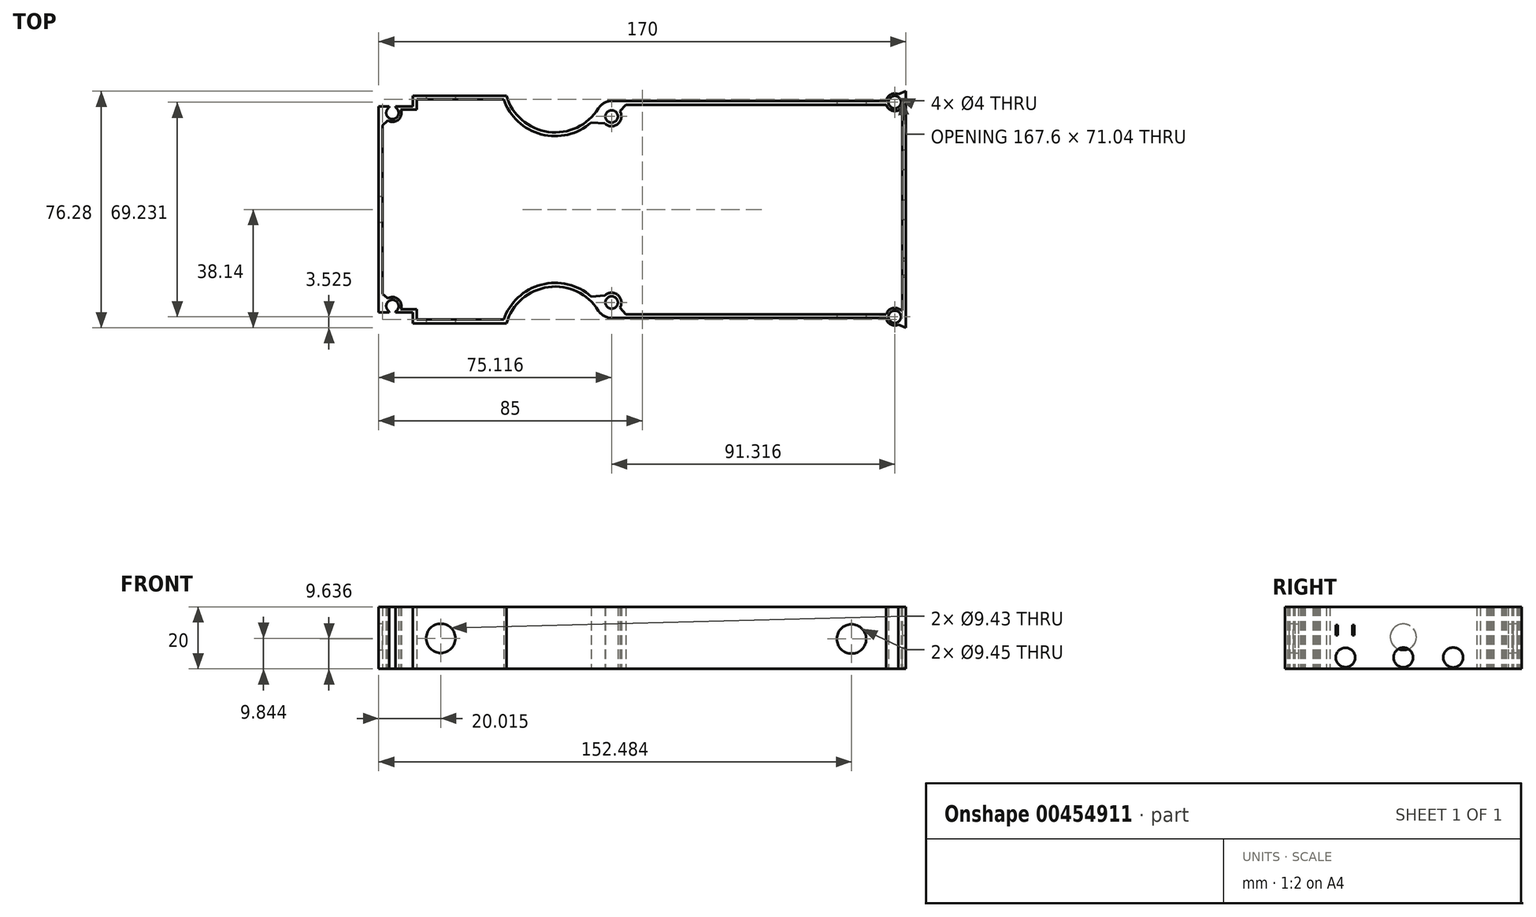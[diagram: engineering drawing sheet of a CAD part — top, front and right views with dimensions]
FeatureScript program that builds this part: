
annotation { "Feature Type Name" : "Feature", "Feature Type Description" : "" }
export const myFeature = defineFeature(function(context is Context, id is Id, definition is map)
    precondition{}
    {
        {
            var Q0;
            Q0=qCreatedBy(makeId("Top.planeOp"),FACE);
            var sketch = newSketch(context, id + "F0", { "sketchPlane" : qUnion([Q0])});
            skLineSegment(sketch, "E0", {"start": v(-2.46, 0) * mm, "end": v(-170, 0) * mm, "construction": true});
            skLineSegment(sketch, "E1.MirrorCS", {"start": v(-164.65, 32.92) * mm, "end": v(-164.65, 33.2) * mm});
            skLineSegment(sketch, "E2.MirrorCS", {"start": v(-166.56, 32.9) * mm, "end": v(-166.56, 33.2) * mm});
            skArc(sketch, "E3.MirrorCS", {"start": v(-5.4, 33.8) * mm, "mid": v(-3.57, 32.62) * mm, "end": v(-1.74, 33.8) * mm});
            skArc(sketch, "E4.MirrorCS", {"start": v(-1.63, 35.13) * mm, "mid": v(-3.57, 36.62) * mm, "end": v(-5.5, 35.13) * mm});
            skLineSegment(sketch, "E5.MirrorCS", {"start": v(-164.65, 33.2) * mm, "end": v(-163.23, 33.2) * mm});
            skLineSegment(sketch, "E6.MirrorCS", {"start": v(-1.2, 32.52) * mm, "end": v(-1.54, 32.57) * mm});
            skCircle(sketch, "E7.MirrorC", {"center": v(-3.57, 34.62) * mm, "radius": 2 * mm});
            skLineSegment(sketch, "E8.MirrorCS", {"start": v(-167.22, 28.48) * mm, "end": v(-167, 28.62) * mm});
            skCircle(sketch, "E9.MirrorC", {"center": v(-94.88, 30) * mm, "radius": 2 * mm});
            skLineSegment(sketch, "E10.MirrorCS", {"start": v(-167.22, 28.48) * mm, "end": v(-168.8, 27.19) * mm});
            skLineSegment(sketch, "E11.MirrorCS", {"start": v(-159, 36.72) * mm, "end": v(-157.8, 36.72) * mm});
            skLineSegment(sketch, "E12.MirrorCS", {"start": v(0, 38.14) * mm, "end": v(0, 35) * mm});
            skLineSegment(sketch, "E13.MirrorCS", {"start": v(-159, 33.2) * mm, "end": v(-159, 36.72) * mm});
            skLineSegment(sketch, "E14.MirrorCS", {"start": v(-155.88, 35.52) * mm, "end": v(-157.8, 35.52) * mm});
            skArc(sketch, "E15.MirrorCS", {"start": v(-166.56, 32.9) * mm, "mid": v(-165.57, 29.15) * mm, "end": v(-164.65, 32.92) * mm});
            skArc(sketch, "E16.MirrorCS", {"start": v(-94.88, 35) * mm, "mid": v(-97.32, 34.37) * mm, "end": v(-99.14, 32.63) * mm});
            skArc(sketch, "E17.MirrorCS", {"start": v(-162.9, 32.23) * mm, "mid": v(-163.68, 28.97) * mm, "end": v(-167, 28.62) * mm});
            skLineSegment(sketch, "E18.MirrorCS", {"start": v(-157.8, 32.23) * mm, "end": v(-162.9, 32.23) * mm});
            skLineSegment(sketch, "E19.MirrorCS", {"start": v(-2.47, 37.17) * mm, "end": v(0, 38.14) * mm});
            skLineSegment(sketch, "E20.MirrorCS", {"start": v(-163.23, 33.2) * mm, "end": v(-159, 33.2) * mm});
            skLineSegment(sketch, "E21.MirrorCS", {"start": v(-157.8, 35.52) * mm, "end": v(-157.8, 32.23) * mm});
            skLineSegment(sketch, "E22.MirrorCS", {"start": v(-170, 33.2) * mm, "end": v(-166.56, 33.2) * mm});
            skLineSegment(sketch, "E23.MirrorCS", {"start": v(-92.23, 31.68) * mm, "end": v(-90.26, 33.8) * mm});
            skLineSegment(sketch, "E24.MirrorCS", {"start": v(-97.1, 27.76) * mm, "end": v(-101.46, 28.05) * mm});
            skLineSegment(sketch, "E25.MirrorCS", {"start": v(-94.88, 35) * mm, "end": v(-6.33, 35) * mm});
            skPoint(sketch, "E26.MirrorP", {"position": v(-170, 36.72) * mm});
            skLineSegment(sketch, "E27.MirrorCS", {"start": v(-90.26, 33.8) * mm, "end": v(-6.33, 33.8) * mm});
            skArc(sketch, "E28.MirrorCS", {"start": v(-97.1, 27.76) * mm, "mid": v(-92.91, 27.55) * mm, "end": v(-92.23, 31.68) * mm});
            skLineSegment(sketch, "E29.MirrorCS", {"start": v(-128.81, 36.72) * mm, "end": v(-157.8, 36.72) * mm});
            skLineSegment(sketch, "E30.MirrorCS", {"start": v(-129.69, 35.52) * mm, "end": v(-155.88, 35.52) * mm});
            skArc(sketch, "E31.MirrorCS", {"start": v(-128.81, 36.72) * mm, "mid": v(-115.3, 25.02) * mm, "end": v(-99.14, 32.63) * mm});
            skPoint(sketch, "E32.MirrorP", {"position": v(-160.88, 35.52) * mm});
            skPoint(sketch, "E33.MirrorP", {"position": v(-97.92, 35) * mm});
            skPoint(sketch, "E34.MirrorP", {"position": v(-166.61, 33.2) * mm});
            skLineSegment(sketch, "E35.MirrorCS", {"start": v(0, 35) * mm, "end": v(0, 0) * mm});
            skLineSegment(sketch, "E36.MirrorCS", {"start": v(-168.8, 0) * mm, "end": v(-168.8, 27.19) * mm});
            skLineSegment(sketch, "E37.MirrorCS", {"start": v(-1.2, 32.52) * mm, "end": v(-1.2, 0) * mm});
            skLineSegment(sketch, "E38.MirrorCS", {"start": v(-170, 0) * mm, "end": v(-170, 33.2) * mm});
            skArc(sketch, "E39.MirrorCS", {"start": v(-129.69, 35.52) * mm, "mid": v(-117.57, 24.25) * mm, "end": v(-101.46, 28.05) * mm});
            skArc(sketch, "E40", {"start": v(-6.33, 35) * mm, "mid": v(-4.94, 37.04) * mm, "end": v(-2.47, 37.17) * mm});
            skArc(sketch, "E41", {"start": v(-6.33, 33.8) * mm, "mid": v(-4.28, 31.83) * mm, "end": v(-1.54, 32.57) * mm});
            skPoint(sketch, "E42.orphan", {"position": v(-5.66, 35) * mm});
            skPoint(sketch, "E43.orphan", {"position": v(-5.54, 33.8) * mm});
            skPoint(sketch, "E44.orphan", {"position": v(-2.57, 32.73) * mm});
            skPoint(sketch, "E45.orphan", {"position": v(-3.57, 36.75) * mm});
            skArc(sketch, "E46.MirrorCS", {"start": v(-1.63, -35.13) * mm, "mid": v(-3.57, -36.62) * mm, "end": v(-5.5, -35.13) * mm});
            skArc(sketch, "E47.MirrorCS", {"start": v(-5.4, -33.8) * mm, "mid": v(-3.57, -32.62) * mm, "end": v(-1.74, -33.8) * mm});
            skLineSegment(sketch, "E48.MirrorCS", {"start": v(-164.65, -32.92) * mm, "end": v(-164.65, -33.2) * mm});
            skCircle(sketch, "E49.MirrorC", {"center": v(-3.57, -34.62) * mm, "radius": 2 * mm});
            skLineSegment(sketch, "E50.MirrorCS", {"start": v(-1.2, -32.52) * mm, "end": v(-1.54, -32.57) * mm});
            skLineSegment(sketch, "E51.MirrorCS", {"start": v(-164.65, -33.2) * mm, "end": v(-163.23, -33.2) * mm});
            skLineSegment(sketch, "E52.MirrorCS", {"start": v(-166.56, -32.9) * mm, "end": v(-166.56, -33.2) * mm});
            skArc(sketch, "E53.MirrorCS", {"start": v(-6.33, -33.8) * mm, "mid": v(-4.28, -31.83) * mm, "end": v(-1.54, -32.57) * mm});
            skLineSegment(sketch, "E54.MirrorCS", {"start": v(-163.23, -33.2) * mm, "end": v(-159, -33.2) * mm});
            skLineSegment(sketch, "E55.MirrorCS", {"start": v(-170, -33.2) * mm, "end": v(-166.56, -33.2) * mm});
            skLineSegment(sketch, "E56.MirrorCS", {"start": v(-157.8, -32.23) * mm, "end": v(-162.9, -32.23) * mm});
            skLineSegment(sketch, "E57.MirrorCS", {"start": v(-167.22, -28.48) * mm, "end": v(-168.8, -27.19) * mm});
            skLineSegment(sketch, "E58.MirrorCS", {"start": v(-167.22, -28.48) * mm, "end": v(-167, -28.62) * mm});
            skLineSegment(sketch, "E59.MirrorCS", {"start": v(-159, -33.2) * mm, "end": v(-159, -36.72) * mm});
            skArc(sketch, "E60.MirrorCS", {"start": v(-166.56, -32.9) * mm, "mid": v(-165.57, -29.15) * mm, "end": v(-164.65, -32.92) * mm});
            skLineSegment(sketch, "E61.MirrorCS", {"start": v(-155.88, -35.52) * mm, "end": v(-157.8, -35.52) * mm});
            skLineSegment(sketch, "E62.MirrorCS", {"start": v(-157.8, -35.52) * mm, "end": v(-157.8, -32.23) * mm});
            skLineSegment(sketch, "E63.MirrorCS", {"start": v(0, -38.14) * mm, "end": v(0, -35) * mm});
            skLineSegment(sketch, "E64.MirrorCS", {"start": v(-159, -36.72) * mm, "end": v(-157.8, -36.72) * mm});
            skCircle(sketch, "E65.MirrorC", {"center": v(-94.88, -30) * mm, "radius": 2 * mm});
            skLineSegment(sketch, "E66.MirrorCS", {"start": v(-2.47, -37.17) * mm, "end": v(0, -38.14) * mm});
            skArc(sketch, "E67.MirrorCS", {"start": v(-6.33, -35) * mm, "mid": v(-4.94, -37.04) * mm, "end": v(-2.47, -37.17) * mm});
            skArc(sketch, "E68.MirrorCS", {"start": v(-162.9, -32.23) * mm, "mid": v(-163.68, -28.97) * mm, "end": v(-167, -28.62) * mm});
            skLineSegment(sketch, "E69.MirrorCS", {"start": v(-97.1, -27.76) * mm, "end": v(-101.46, -28.05) * mm});
            skArc(sketch, "E70.MirrorCS", {"start": v(-94.88, -35) * mm, "mid": v(-97.32, -34.37) * mm, "end": v(-99.14, -32.63) * mm});
            skLineSegment(sketch, "E71.MirrorCS", {"start": v(-92.23, -31.68) * mm, "end": v(-90.26, -33.8) * mm});
            skArc(sketch, "E72.MirrorCS", {"start": v(-97.1, -27.76) * mm, "mid": v(-92.91, -27.55) * mm, "end": v(-92.23, -31.68) * mm});
            skPoint(sketch, "E73.MirrorP", {"position": v(-5.54, -33.8) * mm});
            skPoint(sketch, "E74.MirrorP", {"position": v(-97.92, -35) * mm});
            skLineSegment(sketch, "E75.MirrorCS", {"start": v(-1.2, -32.52) * mm, "end": v(-1.2, 0) * mm});
            skPoint(sketch, "E76.MirrorP", {"position": v(-5.66, -35) * mm});
            skLineSegment(sketch, "E77.MirrorCS", {"start": v(-94.88, -35) * mm, "end": v(-6.33, -35) * mm});
            skLineSegment(sketch, "E78.MirrorCS", {"start": v(-168.8, 0) * mm, "end": v(-168.8, -27.19) * mm});
            skPoint(sketch, "E79.MirrorP", {"position": v(-160.88, -35.52) * mm});
            skPoint(sketch, "E80.MirrorP", {"position": v(-170, -36.72) * mm});
            skPoint(sketch, "E81.MirrorP", {"position": v(-166.61, -33.2) * mm});
            skPoint(sketch, "E82.MirrorP", {"position": v(-2.57, -32.73) * mm});
            skLineSegment(sketch, "E83.MirrorCS", {"start": v(-90.26, -33.8) * mm, "end": v(-6.33, -33.8) * mm});
            skLineSegment(sketch, "E84.MirrorCS", {"start": v(-170, 0) * mm, "end": v(-170, -33.2) * mm});
            skArc(sketch, "E85.MirrorCS", {"start": v(-128.81, -36.72) * mm, "mid": v(-115.3, -25.02) * mm, "end": v(-99.14, -32.63) * mm});
            skArc(sketch, "E86.MirrorCS", {"start": v(-129.69, -35.52) * mm, "mid": v(-117.57, -24.25) * mm, "end": v(-101.46, -28.05) * mm});
            skLineSegment(sketch, "E87.MirrorCS", {"start": v(0, -35) * mm, "end": v(0, 0) * mm});
            skLineSegment(sketch, "E88.MirrorCS", {"start": v(-128.81, -36.72) * mm, "end": v(-157.8, -36.72) * mm});
            skLineSegment(sketch, "E89.MirrorCS", {"start": v(-129.69, -35.52) * mm, "end": v(-155.88, -35.52) * mm});
            skPoint(sketch, "E90.MirrorP", {"position": v(-3.57, -36.75) * mm});
            skSolve(sketch);
        }
        {
            var Q0;
            Q0=makeQuery(id+"F0.imprint","IMPRINT",FACE,{"disambiguationData":[TD([[makeQuery(id+"F0.imprint","IMPRINT",EDGE,{"derivedFrom":sQuery(id+"F0.wireOp",EDGE,"3630c47c-dfee-440a-b75e-d1385f414c443.MirrorCS")}),1.0]])]});
            var Q1;
            Q1=makeQuery(id+"F0.imprint","IMPRINT",FACE,{"disambiguationData":[TD([[makeQuery(id+"F0.imprint","IMPRINT",EDGE,{"derivedFrom":sQuery(id+"F0.wireOp",EDGE,"E1.MirrorCS")}),-1.0]])]});
            extrude(context, id + "F1", {"entities" : qUnion([Q0, Q1]), "depth" : 20 * mm});
        }
        {
            var Q0;
            Q0=makeQuery(id+"F1.opExtrude","SWEPT_FACE",FACE,{"disambiguationData":[OSD([sQuery(id+"F0.wireOp",EDGE,"E64.MirrorCS"),sQuery(id+"F0.wireOp",EDGE,"E88.MirrorCS")])]});
            var sketch = newSketch(context, id + "F2", { "sketchPlane" : qUnion([Q0])});
            skCircle(sketch, "E91", {"center": v(-149.98, 9.84) * mm, "radius": 4.72 * mm});
            skCircle(sketch, "E92", {"center": v(-17.52, 9.64) * mm, "radius": 4.72 * mm});
            skSolve(sketch);
        }
        {
            var Q0;
            Q0 = qSketchRegion(id + "F2", true);
            extrude(context, id + "F3", {"entities" : qUnion([Q0]), "operationType" : NewBodyOperationType.REMOVE, "oppositeDirection" : true, "depth" : 108 * mm});
        }
        {
            var Q0;
            Q0=makeQuery(id+"F1.opExtrude","SWEPT_FACE",FACE,{"disambiguationData":[OSD([sQuery(id+"F0.wireOp",EDGE,"E38.MirrorCS"),sQuery(id+"F0.wireOp",EDGE,"E84.MirrorCS")])]});
            var sketch = newSketch(context, id + "F4", { "sketchPlane" : qUnion([Q0])});
            skCircle(sketch, "E93", {"center": v(0, 10.26) * mm, "radius": 4.2 * mm});
            skPoint(sketch, "E93.centerSnap0", {"position": v(0, 20) * mm});
            skSolve(sketch);
        }
        {
            var Q0;
            Q0=makeQuery(id+"F4.imprint","IMPRINT",FACE,{"disambiguationData":[TD([[makeQuery(id+"F4.imprint","IMPRINT",EDGE,{"derivedFrom":sQuery(id+"F4.wireOp",EDGE,"E93")}),1.0]])]});
            extrude(context, id + "F5", {"entities" : qUnion([Q0]), "operationType" : NewBodyOperationType.REMOVE, "oppositeDirection" : true, "depth" : 25 * mm});
        }
        {
            var Q0;
            Q0=makeQuery(id+"F1.opExtrude","SWEPT_FACE",FACE,{"disambiguationData":[OSD([sQuery(id+"F0.wireOp",EDGE,"E12.MirrorCS"),sQuery(id+"F0.wireOp",EDGE,"E35.MirrorCS"),sQuery(id+"F0.wireOp",EDGE,"E63.MirrorCS"),sQuery(id+"F0.wireOp",EDGE,"E87.MirrorCS")])]});
            var sketch = newSketch(context, id + "F6", { "sketchPlane" : qUnion([Q0])});
            skCircle(sketch, "E94", {"center": v(0, 3.67) * mm, "radius": 3.17 * mm});
            skPoint(sketch, "E95", {"position": v(0, 20) * mm});
            skCircle(sketch, "E96", {"center": v(16.07, 3.67) * mm, "radius": 3.2 * mm});
            skCircle(sketch, "E97", {"center": v(-18.65, 3.67) * mm, "radius": 3.13 * mm});
            skLineSegment(sketch, "E98.bottom", {"start": v(-21.73, 14.09) * mm, "end": v(-21.12, 14.09) * mm});
            skLineSegment(sketch, "E98.top", {"start": v(-21.73, 10.86) * mm, "end": v(-21.12, 10.86) * mm});
            skLineSegment(sketch, "E98.left", {"start": v(-21.73, 14.09) * mm, "end": v(-21.73, 10.86) * mm});
            skLineSegment(sketch, "E98.right", {"start": v(-21.12, 14.09) * mm, "end": v(-21.12, 10.86) * mm});
            skLineSegment(sketch, "E99.bottom", {"start": v(-16.5, 10.86) * mm, "end": v(-15.84, 10.86) * mm});
            skLineSegment(sketch, "E99.top", {"start": v(-16.5, 14.09) * mm, "end": v(-15.84, 14.09) * mm});
            skLineSegment(sketch, "E99.left", {"start": v(-16.5, 10.86) * mm, "end": v(-16.5, 14.09) * mm});
            skLineSegment(sketch, "E99.right", {"start": v(-15.84, 10.86) * mm, "end": v(-15.84, 14.09) * mm});
            skSolve(sketch);
        }
        {
            var Q0;
            Q0 = qSketchRegion(id + "F6", true);
            extrude(context, id + "F7", {"entities" : qUnion([Q0]), "operationType" : NewBodyOperationType.REMOVE, "oppositeDirection" : true, "depth" : 25 * mm});
        }
    });
